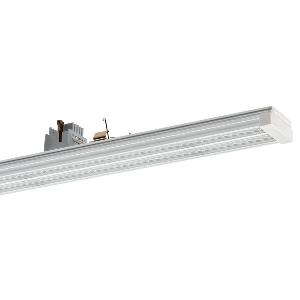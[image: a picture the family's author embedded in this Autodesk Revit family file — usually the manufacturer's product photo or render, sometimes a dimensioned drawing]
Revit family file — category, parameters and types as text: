
# Revit family: conveo_-_cvg_15000_840_xn-l_ea_5_226848479-00804986_b442
name_source: partatom
category: Lighting Fixtures
units: mm (PartAtom-declared; Revit-internal decimal feet)

## family parameters
Cut with Voids When Loaded = No
Host = Face
Light Source = No
Part Type = Normal
Room Calculation Point = No
Round Connector Dimension = Use Diameter
Shared = No

## types (1)
- CONVEO - CVG 15000/840/xN-L/EA/5 (1 x LED, 15400 lm, 4000K)
    Apparent Load = 95 VA
    Approval mark = CE
    CIE Flux Codes = 86 95 99 100 100
    Color Rendering = 80-89
    Color Temperature = 4000K
    Control Gear = Electronic ballast
    Default Elevation = 1800 mm
    Description = CVG 15000/840/xN-L/EA/5|Continuous-row system|light source: LED|work equipment: Electronic ballast|connected load: 220-240 V, 50-60 Hz|Power consumption: approx. 95 W|luminous flux: 15400 lm|luminous efficacy: 162 lm/W|colour temperature: Cold white, ca. 4000 K|color rendering index (CRI): >= 80|chromaticity tolerance:  3 SDCM|System of protection: IP 54|class of protection: I|technology: Switchable|luminaire body|material: Aluminium|surface: Powder coatet|colour: White|lamp cover: Acrylic (PMMA), Satine|weight (net): approx. 2.2 kg|Fastening: Available separately|maximum ambient temperature: 41 ░C|glare control: Lens optics|Approval mark: VDE - ENEC|
    Frequency = 50 Hz
    Height = 70 mm
    Lamp = 1 x LED
    Lamp Light Flux = 15400 lm
    Lamp count = 1
    Length = 1500 mm
    Luminous efficacy = 162 lm/W
    Manufacturer = Waldmann
    ModVariant = No
    Model = 226848479-00804986
    Mounting Place = Ceiling
    Mounting Type = Pendant
    Number of Poles = 1
    OnlyDefault = Yes
    Power Factor = 1
    Product Name = CONVEO - CVG 15000/840/xN-L/EA/5
    Product group = Continuous-row system (industry)
    ProductGroupID = 301
    Protection Class = Protection class I
    Protection Degree = IP 54
    RLX_Detail_Level = 1
    RlxData = <blob elided: 135317 chars, md5=d9e1176f>
    Socket = socket
    Standby Power = 0 W
    System Light Flux = 15400 lm
    System Power = 95 W
    Type Comments = Product without accessories
    Type Image = 226848359-00804974-2l5.jpg
    URL = http://relux.com
    VarID = ---
    Voltage = 230 V
    Voltage Range = 220-240 V
    Weight = 0.00 kg
    Width = 64 mm

## geometry (parser evidence)
native form markers: Blend x4, Sweep x10
no freeform markers — native parametric forms only
